# Revit family: Haworth_Planes_TrainingTable_HalfRound_AP_PRELIMINARY
name_source: partatom
category: Furniture
units: mm (PartAtom-declared; Revit-internal decimal feet)

## family parameters
Always vertical = Yes
Cut with Voids When Loaded = No
OmniClass Number = 23.40.70.14.64.21
OmniClass Title = Systems Furniture
Room Calculation Point = No
Shared = No
Work Plane-Based = No

## types (1)
- 1500w x 750d
    Actual Depth = 750 mm  [stored 2.46063 ft]
    Actual Height = 740 mm  [stored 2.42782 ft]
    Actual Width = 1500 mm  [stored 4.92126 ft]
    Assembly Code = E2020200
    Base Width = 1000 mm  [stored 3.28084 ft]
    Caster Finish = Haworth _ Polymer _ Black
    Casters = No
    Description = Haworth - Planes - Training Table - Half-Round
    Flip Top = Yes
    Flip Top Finish = Haworth _ Paint _ Undecided _ Table
    Glides = Yes
    Leg Height = 715 mm  [stored 2.3458 ft]
    Manufacturer = Haworth
    Model = WOPLTRF
    Revision Number = 1
    Screen Width = 1310 mm  [stored 4.2979 ft]
    Size = Verify Final Dim. w/ Haworth
    Trim Finish = Haworth _ Polymer _ Undecided
    URL = https://www.haworth.com
    URL - Product = https://www.haworth.com
    Warranty = http://www.haworth.com
    With Screen = Yes

note: [stored X ft] marks values corroborated as IEEE doubles in the binary element streams (Revit-internal decimal feet)

## geometry (parser evidence)
native form markers: Sweep x16
no freeform markers — native parametric forms only
